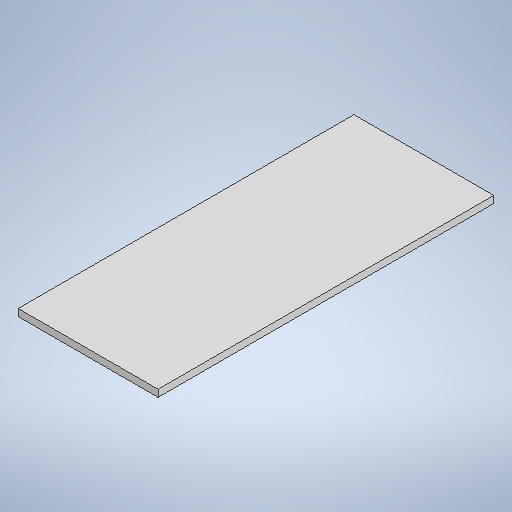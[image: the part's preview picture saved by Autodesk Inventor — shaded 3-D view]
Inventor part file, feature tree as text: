
AUTODESK INVENTOR PART (.ipt)
format: ipt  version: 2025 (Build 290162010, 162A)  size: 216,064 bytes
history: native  units: in
note: dims shown in document units (in); Inventor stores cm internally (conversion verified against a paired STEP export)
features: extrude x1, sketch x1
ambient origin geometry x8: Origin, YZ Plane, XZ Plane, XY Plane, X Axis, Y Axis, Z Axis, Center Point
bodies: Solid1 (feature_tree)
feature tree (2):
  extrude  "Extrusion1"  Depth=12.0in
  sketch  "Sketch1"  dims[d0=5.0in d1=12.0in d2=0.25in d3=0.0in]
